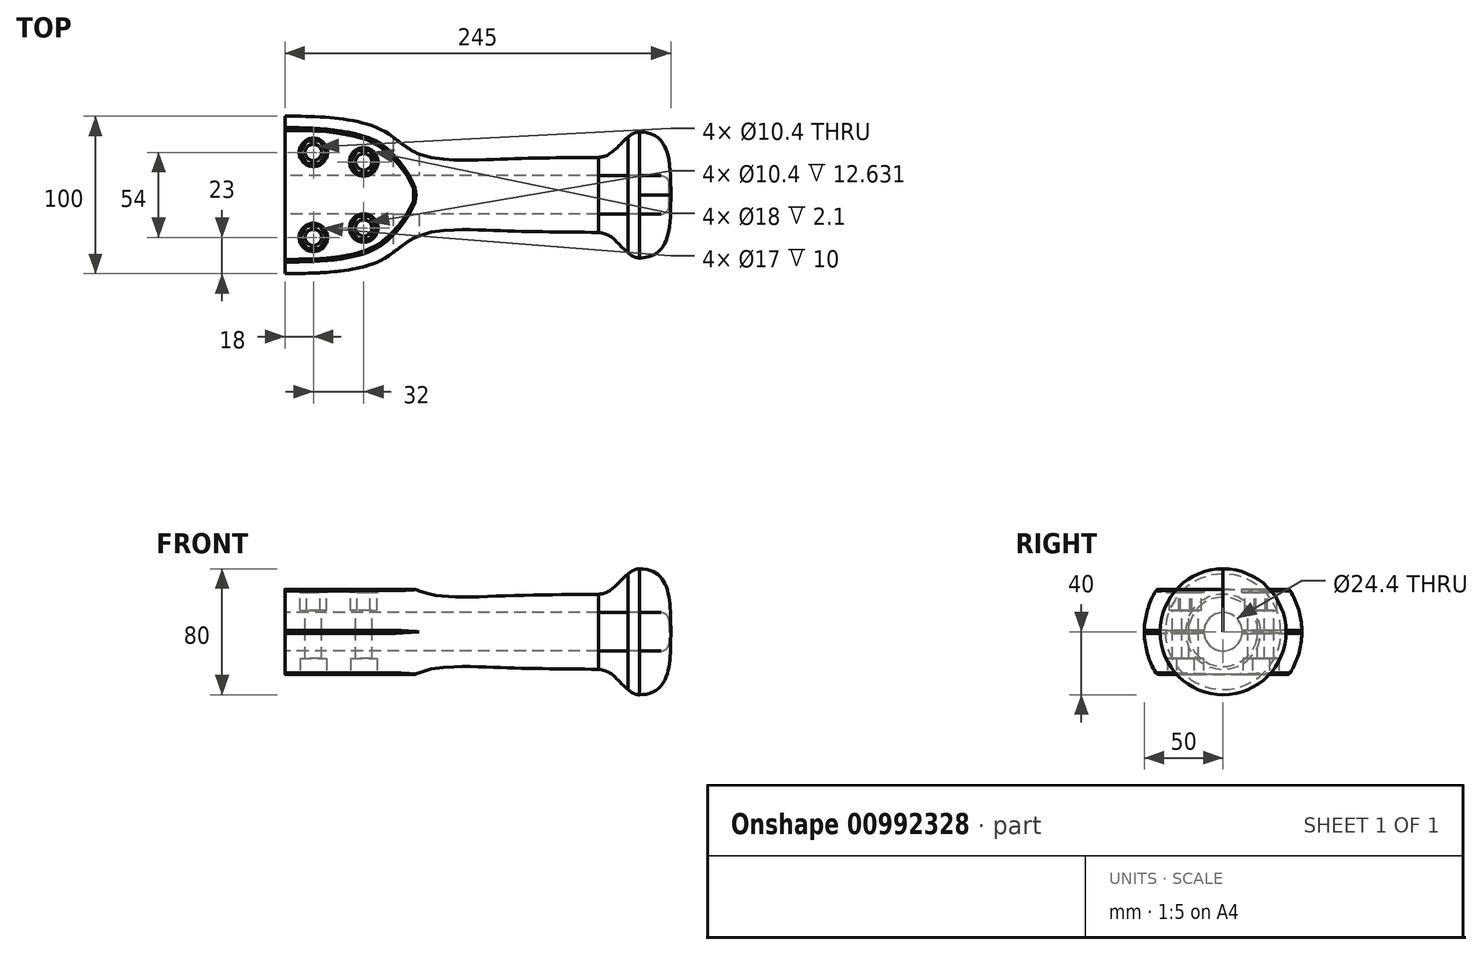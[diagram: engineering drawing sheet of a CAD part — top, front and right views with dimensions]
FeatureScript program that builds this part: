
annotation { "Feature Type Name" : "Feature", "Feature Type Description" : "" }
export const myFeature = defineFeature(function(context is Context, id is Id, definition is map)
    precondition{}
    {
        {
            var Q0;
            Q0=qCreatedBy(makeId("Front.planeOp"),FACE);
            var sketch = newSketch(context, id + "F0", { "sketchPlane" : qUnion([Q0])});
            skLineSegment(sketch, "E0", {"start": v(0, 50) * mm, "end": v(0, 0) * mm});
            skLineSegment(sketch, "E1", {"start": v(0, 0) * mm, "end": v(245, 0) * mm});
            skLineSegment(sketch, "E2", {"start": v(85, 0) * mm, "end": v(85, 26) * mm, "construction": true});
            skLineSegment(sketch, "E3", {"start": v(145, 0) * mm, "end": v(145, 23) * mm, "construction": true});
            skLineSegment(sketch, "E4", {"start": v(205, 0) * mm, "end": v(205, 24) * mm, "construction": true});
            skLineSegment(sketch, "E5", {"start": v(225, 0) * mm, "end": v(225, 40) * mm, "construction": true});
            skLineSegment(sketch, "E6", {"start": v(60, 42) * mm, "end": v(60, 0) * mm, "construction": true});
            skFitSpline(sketch, "E7", {"points": [v(0, 50) * mm, v(60, 42) * mm, v(85, 26) * mm, v(145, 23) * mm, v(205, 24) * mm], "startDerivative": vector(265.83, 0) * mm, "endDerivative": vector(46.28, 3.62) * mm});
            skLineSegment(sketch, "E8", {"start": v(85, 26) * mm, "end": v(85, 0) * mm});
            skLineSegment(sketch, "E9", {"start": v(0, 0) * mm, "end": v(85, 0) * mm});
            skLineSegment(sketch, "E10", {"start": v(205, 24) * mm, "end": v(205, 0) * mm});
            skPoint(sketch, "E11.middle", {"position": v(225, 0) * mm});
            skLineSegment(sketch, "E12.right", {"start": v(205, 15) * mm, "end": v(205, 0) * mm, "construction": true});
            skLineSegment(sketch, "E13", {"start": v(-11.82, 108.17) * mm, "end": v(-11.82, 58.17) * mm, "construction": true});
            skLineSegment(sketch, "E14", {"start": v(-11.82, 58.17) * mm, "end": v(233.18, 58.17) * mm, "construction": true});
            skLineSegment(sketch, "E15", {"start": v(73.18, 58.17) * mm, "end": v(73.18, 84.17) * mm, "construction": true});
            skLineSegment(sketch, "E16", {"start": v(133.18, 58.17) * mm, "end": v(133.18, 82.17) * mm, "construction": true});
            skLineSegment(sketch, "E17", {"start": v(48.18, 100.17) * mm, "end": v(48.18, 58.17) * mm, "construction": true});
            skFitSpline(sketch, "E18", {"points": [v(-11.82, 108.17) * mm, v(48.18, 100.17) * mm, v(73.18, 84.17) * mm, v(133.18, 82.17) * mm, v(193.18, 80.17) * mm], "startDerivative": vector(265.83, 0) * mm, "endDerivative": vector(46.66, -3.23) * mm, "construction": true});
            skLineSegment(sketch, "E19", {"start": v(73.18, 84.17) * mm, "end": v(73.18, 58.17) * mm, "construction": true});
            skLineSegment(sketch, "E20", {"start": v(-11.82, 58.17) * mm, "end": v(73.18, 58.17) * mm, "construction": true});
            skLineSegment(sketch, "E21", {"start": v(233.18, 58.17) * mm, "end": v(193.18, 58.17) * mm, "construction": true});
            skPoint(sketch, "E22.middle", {"position": v(213.18, 58.17) * mm});
            skLineSegment(sketch, "E23.bottom", {"start": v(227.18, 58.17) * mm, "end": v(233.18, 58.17) * mm, "construction": true});
            skLineSegment(sketch, "E24.right", {"start": v(193.18, 73.17) * mm, "end": v(193.18, 58.17) * mm, "construction": true});
            skFitSpline(sketch, "E25", {"points": [v(213.18, 98.17) * mm, v(233.18, 58.17) * mm], "startDerivative": vector(60, 0) * mm, "endDerivative": vector(0, -60) * mm, "construction": true});
            skLineSegment(sketch, "E26.top", {"start": v(213.18, 98.17) * mm, "end": v(233.18, 98.17) * mm, "construction": true});
            skLineSegment(sketch, "E26.left", {"start": v(213.18, 58.17) * mm, "end": v(213.18, 98.17) * mm, "construction": true});
            skLineSegment(sketch, "E26.right", {"start": v(233.18, 58.17) * mm, "end": v(233.18, 98.17) * mm, "construction": true});
            skFitSpline(sketch, "E27.MirrorCS", {"points": [v(213.18, 98.17) * mm, v(193.16, 58.15) * mm], "startDerivative": vector(-60, 0) * mm, "endDerivative": vector(-0.03, -60) * mm, "construction": true});
            skCircle(sketch, "E28", {"center": v(193.18, 80.17) * mm, "radius": 6 * mm, "construction": true});
            skFitSpline(sketch, "E29", {"points": [v(187.19, 80.56) * mm, v(195.66, 85.63) * mm], "startDerivative": vector(14.26, -0.68) * mm, "endDerivative": vector(2.5, 8.39) * mm, "construction": true});
            skLineSegment(sketch, "E30.bottom", {"start": v(213.18, 98.17) * mm, "end": v(193.18, 98.17) * mm, "construction": true});
            skLineSegment(sketch, "E30.top", {"start": v(213.18, 58.17) * mm, "end": v(193.18, 58.17) * mm, "construction": true});
            skLineSegment(sketch, "E30.left", {"start": v(213.18, 98.17) * mm, "end": v(213.18, 58.17) * mm, "construction": true});
            skLineSegment(sketch, "E31.bottom", {"start": v(193.18, 58.17) * mm, "end": v(233.17, 58.17) * mm, "construction": true});
            skLineSegment(sketch, "E31.top", {"start": v(193.18, 98.17) * mm, "end": v(233.18, 98.17) * mm, "construction": true});
            skLineSegment(sketch, "E31.right", {"start": v(233.17, 58.17) * mm, "end": v(233.18, 98.17) * mm, "construction": true});
            skLineSegment(sketch, "E32", {"start": v(193.18, 58.17) * mm, "end": v(233.18, 58.17) * mm, "construction": true});
            skFitSpline(sketch, "E33.MirrorCS", {"points": [v(213.18, 98.17) * mm, v(193.1, 58.17) * mm], "startDerivative": vector(-60, 0) * mm, "endDerivative": vector(0, -60) * mm, "construction": true});
            skFitSpline(sketch, "E34.MirrorCS", {"points": [v(213.18, 98.17) * mm, v(193.18, 58.17) * mm], "startDerivative": vector(-60, 0) * mm, "endDerivative": vector(0, -60) * mm, "construction": true});
            skLineSegment(sketch, "E35.bottom", {"start": v(245, 0) * mm, "end": v(205, 0) * mm, "construction": true});
            skLineSegment(sketch, "E35.top", {"start": v(245, 20) * mm, "end": v(205, 20) * mm, "construction": true});
            skLineSegment(sketch, "E35.left", {"start": v(245, 0) * mm, "end": v(245, 20) * mm, "construction": true});
            skLineSegment(sketch, "E35.right", {"start": v(205, 0) * mm, "end": v(205, 20) * mm, "construction": true});
            skLineSegment(sketch, "E36.bottom", {"start": v(225, 40) * mm, "end": v(245, 40) * mm, "construction": true});
            skLineSegment(sketch, "E36.top", {"start": v(225, 0) * mm, "end": v(245, 0) * mm, "construction": true});
            skLineSegment(sketch, "E36.left", {"start": v(225, 40) * mm, "end": v(225, 0) * mm, "construction": true});
            skLineSegment(sketch, "E36.right", {"start": v(245, 40) * mm, "end": v(245, 0) * mm, "construction": true});
            skFitSpline(sketch, "E37", {"points": [v(225, 40) * mm, v(245, 0) * mm], "startDerivative": vector(60, 0) * mm, "endDerivative": vector(0, -60) * mm});
            skLineSegment(sketch, "E38.bottom", {"start": v(225, 40) * mm, "end": v(205, 40) * mm, "construction": true});
            skLineSegment(sketch, "E38.top", {"start": v(225, 0) * mm, "end": v(205, 0) * mm, "construction": true});
            skLineSegment(sketch, "E38.right", {"start": v(205, 40) * mm, "end": v(205, 0) * mm, "construction": true});
            skCircle(sketch, "E39", {"center": v(195.66, 85.63) * mm, "radius": 2.92 * mm, "construction": true});
            skCircle(sketch, "E40", {"center": v(187.19, 80.56) * mm, "radius": 4.76 * mm, "construction": true});
            skFitSpline(sketch, "E41", {"points": [v(205, 0) * mm, v(225, 40) * mm], "startDerivative": vector(0, 60) * mm, "endDerivative": vector(30, 0) * mm});
            skFitSpline(sketch, "E42", {"points": [v(199, 23.84) * mm, v(217.81, 36.7) * mm], "startDerivative": vector(27.62, 1.67) * mm, "endDerivative": vector(18.82, 14.57) * mm});
            skLineSegment(sketch, "E43", {"start": v(217.81, 36.7) * mm, "end": v(180.43, -0.9) * mm, "construction": true});
            skLineSegment(sketch, "E44", {"start": v(214.8, 34.03) * mm, "end": v(210.87, 29.97) * mm, "construction": true});
            skLineSegment(sketch, "E45", {"start": v(205, 24) * mm, "end": v(79, 21.9) * mm, "construction": true});
            skLineSegment(sketch, "E46", {"start": v(79, 34.04) * mm, "end": v(79, 14.16) * mm, "construction": true});
            skLineSegment(sketch, "E47", {"start": v(106.67, 22.36) * mm, "end": v(107.04, 0) * mm, "construction": true});
            skLineSegment(sketch, "E48", {"start": v(107.04, 0) * mm, "end": v(106.67, 0.95) * mm, "construction": true});
            skSolve(sketch);
        }
        {
            var Q0;
            {var subQ0=sQuery(id+"F0.wireOp",EDGE,"E0");Q0=makeQuery(id+"F0.imprint","IMPRINT",FACE,{"disambiguationData":[TD([[makeQuery(id+"F0.imprint","IMPRINT",EDGE,{"derivedFrom":subQ0}),1.0]])]});}
            var Q1;
            {var subQ3=sQuery(id+"F0.wireOp",EDGE,"E8");Q1=makeQuery(id+"F0.imprint","IMPRINT",FACE,{"disambiguationData":[TD([[makeQuery(id+"F0.imprint","IMPRINT",EDGE,{"derivedFrom":subQ3}),1.0]])]});}
            var Q2;
            {var subQ0=sQuery(id+"F0.wireOp",EDGE,"E37");Q2=makeQuery(id+"F0.imprint","IMPRINT",FACE,{"disambiguationData":[TD([[makeQuery(id+"F0.imprint","IMPRINT",EDGE,{"derivedFrom":subQ0}),-1.0]])]});}
            var Q3;
            {var subQ0=sQuery(id+"F0.wireOp",EDGE,"E10");Q3=makeQuery(id+"F0.imprint","IMPRINT",FACE,{"disambiguationData":[TD([[makeQuery(id+"F0.imprint","IMPRINT",EDGE,{"derivedFrom":subQ0}),1.0]])]});}
            var Q4;
            Q4=sQuery(id+"F0.wireOp",EDGE,"E1");
            revolve(context, id + "F1", {"surfaceOperationType" : NewSurfaceOperationType.NEW, "entities" : qUnion([Q0, Q1, Q2, Q3]), "axis" : qUnion([Q4]), "revolveType" : RevolveType.FULL});
        }
        {
            var Q0;
            Q0=qCreatedBy(makeId("Right.planeOp"),FACE);
            cPlane(context, id + "F2", {"entities" : qUnion([Q0]), "cplaneType" : CPlaneType.OFFSET, "offset" : 90 * mm, "width" : 150 * mm, "height" : 150 * mm});
        }
        {
            var Q0;
            Q0=qCreatedBy(id+"F2.planeOp",FACE);
            var sketch = newSketch(context, id + "F3", { "sketchPlane" : qUnion([Q0])});
            skLineSegment(sketch, "E49.bottom", {"start": v(-65.87, 27) * mm, "end": v(58.89, 27) * mm});
            skLineSegment(sketch, "E49.top", {"start": v(-65.87, -27) * mm, "end": v(58.89, -27) * mm});
            skLineSegment(sketch, "E49.left", {"start": v(-65.87, 27) * mm, "end": v(-65.87, -27) * mm});
            skLineSegment(sketch, "E49.right", {"start": v(58.89, 27) * mm, "end": v(58.89, -27) * mm});
            skPoint(sketch, "E49.middle", {"position": v(-3.5, 0) * mm});
            skLineSegment(sketch, "E50.bottom", {"start": v(-135.82, 62.52) * mm, "end": v(135.82, 62.52) * mm});
            skLineSegment(sketch, "E50.top", {"start": v(-135.82, -80.38) * mm, "end": v(135.82, -80.38) * mm});
            skLineSegment(sketch, "E50.left", {"start": v(-135.82, 62.52) * mm, "end": v(-135.82, -80.38) * mm});
            skLineSegment(sketch, "E50.right", {"start": v(135.82, 62.52) * mm, "end": v(135.82, -80.38) * mm});
            skPoint(sketch, "E50.middle", {"position": v(0, -8.93) * mm});
            skSolve(sketch);
        }
        {
            var Q0;
            Q0=makeQuery(id+"F3.imprint","IMPRINT",FACE,{"disambiguationData":[TD([[makeQuery(id+"F3.imprint","IMPRINT",EDGE,{"derivedFrom":sQuery(id+"F3.wireOp",EDGE,"E49.bottom")}),1.0]])]});
            extrude(context, id + "F4", {"entities" : qUnion([Q0]), "operationType" : NewBodyOperationType.REMOVE, "oppositeDirection" : true, "depth" : 139 * mm, "offsetDistance" : 25 * mm});
        }
        {
            var Q0;
            Q0=makeQuery(id+"F4.boolean.opBoolean","INTERSECT",EDGE,{"derivedFrom":[makeQuery(id+"F1.opRevolve","SWEPT_FACE",FACE,{"disambiguationData":[OSD([sQuery(id+"F0.wireOp",EDGE,"E7")])]}),makeQuery(id+"F4.opExtrude","SWEPT_FACE",FACE,{"disambiguationData":[OSD([sQuery(id+"F3.wireOp",EDGE,"E49.bottom")])]})]});
            var Q1;
            Q1=makeQuery(id+"F4.boolean.opBoolean","INTERSECT",EDGE,{"derivedFrom":[makeQuery(id+"F1.opRevolve","SWEPT_FACE",FACE,{"disambiguationData":[OSD([sQuery(id+"F0.wireOp",EDGE,"E7")])]}),makeQuery(id+"F4.opExtrude","SWEPT_FACE",FACE,{"disambiguationData":[OSD([sQuery(id+"F3.wireOp",EDGE,"E49.top")])]})]});
            fillet(context, id + "F5", {"entities" : qUnion([Q0, Q1]), "radius" : 2 * mm, "tangentPropagation" : true, "defaultsChanged" : true, "vertexSettings" : [], "allowEdgeOverflow" : false});
        }
        {
            var Q0;
            Q0=makeQuery(id+"F4.boolean.opBoolean","COPY",FACE,{"derivedFrom":makeQuery(id+"F4.opExtrude","SWEPT_FACE",FACE,{"disambiguationData":[OSD([sQuery(id+"F3.wireOp",EDGE,"E49.bottom")])]})});
            var sketch = newSketch(context, id + "F6", { "sketchPlane" : qUnion([Q0])});
            skLineSegment(sketch, "E51", {"start": v(0, 0) * mm, "end": v(79.24, 0) * mm, "construction": true});
            skCircle(sketch, "E52.cCircle", {"center": v(50, 21) * mm, "radius": 7.2 * mm, "construction": true});
            skLineSegment(sketch, "E52.0", {"start": v(54.16, 28.2) * mm, "end": v(58.31, 21) * mm});
            skLineSegment(sketch, "E52.1", {"start": v(58.31, 21) * mm, "end": v(54.16, 13.8) * mm});
            skLineSegment(sketch, "E52.2", {"start": v(54.16, 13.8) * mm, "end": v(45.84, 13.8) * mm});
            skLineSegment(sketch, "E52.3", {"start": v(45.84, 13.8) * mm, "end": v(41.69, 21) * mm});
            skLineSegment(sketch, "E52.4", {"start": v(41.69, 21) * mm, "end": v(45.84, 28.2) * mm});
            skLineSegment(sketch, "E52.5", {"start": v(45.84, 28.2) * mm, "end": v(54.16, 28.2) * mm});
            skPoint(sketch, "E52.0.midPoint", {"position": v(56.24, 24.6) * mm});
            skCircle(sketch, "E53.cCircle", {"center": v(18, 27) * mm, "radius": 7.2 * mm, "construction": true});
            skLineSegment(sketch, "E53.0", {"start": v(13.84, 34.2) * mm, "end": v(22.16, 34.2) * mm});
            skLineSegment(sketch, "E53.1", {"start": v(22.16, 34.2) * mm, "end": v(26.31, 27) * mm});
            skLineSegment(sketch, "E53.2", {"start": v(26.31, 27) * mm, "end": v(22.16, 19.8) * mm});
            skLineSegment(sketch, "E53.3", {"start": v(22.16, 19.8) * mm, "end": v(13.84, 19.8) * mm});
            skLineSegment(sketch, "E53.4", {"start": v(13.84, 19.8) * mm, "end": v(9.69, 27) * mm});
            skLineSegment(sketch, "E53.5", {"start": v(9.69, 27) * mm, "end": v(13.84, 34.2) * mm});
            skPoint(sketch, "E53.0.midPoint", {"position": v(18, 34.2) * mm});
            skPoint(sketch, "E54.cCircle.perimeterSnap0", {"position": v(24.24, 30.6) * mm});
            skPoint(sketch, "E54.0.midPoint.positionSnap0", {"position": v(24.24, 30.6) * mm});
            skFitSpline(sketch, "E55.0", {"points": [v(0, -39.26) * mm, v(4.13, -39.26) * mm, v(10.34, -39.2) * mm, v(18.6, -38.88) * mm, v(24.78, -38.5) * mm, v(30.96, -37.92) * mm, v(36.08, -37.22) * mm, v(40.14, -36.5) * mm, v(43.17, -35.87) * mm, v(45.68, -35.24) * mm, v(47.67, -34.67) * mm, v(49.65, -34.05) * mm, v(52.07, -33.19) * mm, v(54.9, -31.97) * mm, v(57.18, -30.78) * mm, v(58.94, -29.69) * mm, v(60.23, -28.8) * mm, v(61.47, -27.86) * mm, v(63.08, -26.55) * mm, v(64.98, -24.82) * mm, v(67.15, -22.63) * mm, v(69.24, -20.36) * mm, v(71.26, -18.02) * mm, v(73.24, -15.64) * mm, v(75.17, -13.21) * mm, v(77.03, -10.74) * mm, v(78.5, -8.61) * mm, v(79.56, -6.84) * mm, v(80.28, -5.46) * mm, v(80.9, -4.04) * mm, v(81.29, -2.8) * mm, v(81.5, -1.78) * mm, v(81.65, -0.76) * mm, v(81.68, 0.53) * mm, v(81.48, 2.09) * mm, v(81.06, 3.58) * mm, v(80.5, 5.01) * mm, v(79.8, 6.41) * mm, v(79.02, 7.75) * mm, v(77.92, 9.47) * mm, v(76.43, 11.56) * mm, v(74.56, 14) * mm, v(72.62, 16.4) * mm, v(70.64, 18.75) * mm, v(68.6, 21.06) * mm, v(66.5, 23.3) * mm, v(64.32, 25.45) * mm, v(62.4, 27.13) * mm, v(60.78, 28.4) * mm, v(59.52, 29.3) * mm, v(58.21, 30.15) * mm, v(56.88, 30.92) * mm, v(55.53, 31.63) * mm, v(53.69, 32.5) * mm, v(51.34, 33.47) * mm, v(48.46, 34.45) * mm, v(45.52, 35.3) * mm, v(42.53, 36.01) * mm, v(39.52, 36.62) * mm, v(35.5, 37.3) * mm, v(30.46, 37.97) * mm, v(22.37, 38.7) * mm, v(12.22, 39.17) * mm, v(4.07, 39.26) * mm, v(0, 39.26) * mm]});
            skLineSegment(sketch, "E56.bottom", {"start": v(50, 21) * mm, "end": v(18, 21) * mm, "construction": true});
            skLineSegment(sketch, "E57.MirrorCS", {"start": v(54.16, -28.2) * mm, "end": v(58.31, -21) * mm});
            skPoint(sketch, "E58.MirrorP", {"position": v(24.24, -30.6) * mm});
            skLineSegment(sketch, "E59.MirrorCS", {"start": v(41.69, -21) * mm, "end": v(45.84, -28.2) * mm});
            skPoint(sketch, "E60.MirrorP", {"position": v(18, -34.2) * mm});
            skLineSegment(sketch, "E61.MirrorCS", {"start": v(13.84, -34.2) * mm, "end": v(22.16, -34.2) * mm});
            skLineSegment(sketch, "E62.MirrorCS", {"start": v(9.69, -27) * mm, "end": v(13.84, -34.2) * mm});
            skLineSegment(sketch, "E63.MirrorCS", {"start": v(22.16, -19.8) * mm, "end": v(13.84, -19.8) * mm});
            skLineSegment(sketch, "E64.MirrorCS", {"start": v(45.84, -13.8) * mm, "end": v(41.69, -21) * mm});
            skPoint(sketch, "E65.MirrorP", {"position": v(56.24, -24.6) * mm});
            skLineSegment(sketch, "E66.MirrorCS", {"start": v(54.16, -13.8) * mm, "end": v(45.84, -13.8) * mm});
            skLineSegment(sketch, "E67.MirrorCS", {"start": v(58.31, -21) * mm, "end": v(54.16, -13.8) * mm});
            skLineSegment(sketch, "E68.MirrorCS", {"start": v(50, -21) * mm, "end": v(18, -21) * mm, "construction": true});
            skLineSegment(sketch, "E69.MirrorCS", {"start": v(13.84, -19.8) * mm, "end": v(9.69, -27) * mm});
            skCircle(sketch, "E70.MirrorC", {"center": v(18, -27) * mm, "radius": 7.2 * mm, "construction": true});
            skLineSegment(sketch, "E71.MirrorCS", {"start": v(22.16, -34.2) * mm, "end": v(26.31, -27) * mm});
            skLineSegment(sketch, "E72.MirrorCS", {"start": v(26.31, -27) * mm, "end": v(22.16, -19.8) * mm});
            skCircle(sketch, "E73.MirrorC", {"center": v(50, -21) * mm, "radius": 7.2 * mm, "construction": true});
            skLineSegment(sketch, "E74.MirrorCS", {"start": v(45.84, -28.2) * mm, "end": v(54.16, -28.2) * mm});
            skSolve(sketch);
        }
        {
            var Q0;
            Q0=qSketchRegion(id+"F6",true);
            extrude(context, id + "F7", {"entities" : qUnion([Q0]), "operationType" : NewBodyOperationType.REMOVE, "oppositeDirection" : true, "depth" : 13.4 * mm, "offsetDistance" : 25 * mm});
        }
        {
            var Q0;
            Q0=makeQuery(id+"F4.boolean.opBoolean","COPY",FACE,{"derivedFrom":makeQuery(id+"F4.opExtrude","SWEPT_FACE",FACE,{"disambiguationData":[OSD([sQuery(id+"F3.wireOp",EDGE,"E49.bottom")])]})});
            var sketch = newSketch(context, id + "F8", { "sketchPlane" : qUnion([Q0])});
            skCircle(sketch, "E75.20", {"center": v(18, 27) * mm, "radius": 9 * mm});
            skCircle(sketch, "E75.21", {"center": v(50, 21) * mm, "radius": 9 * mm});
            skLineSegment(sketch, "E76", {"start": v(0, 0) * mm, "end": v(82.32, 0) * mm, "construction": true});
            skCircle(sketch, "E77.MirrorC", {"center": v(18, -27) * mm, "radius": 9 * mm});
            skCircle(sketch, "E78.MirrorC", {"center": v(50, -21) * mm, "radius": 9 * mm});
            skLineSegment(sketch, "E79", {"start": v(13.84, 34.2) * mm, "end": v(22.16, 19.8) * mm, "construction": true});
            skLineSegment(sketch, "E80", {"start": v(45.84, 28.2) * mm, "end": v(54.16, 13.8) * mm, "construction": true});
            skSolve(sketch);
        }
        {
            var Q0;
            Q0=qSketchRegion(id+"F8",true);
            extrude(context, id + "F9", {"entities" : qUnion([Q0]), "operationType" : NewBodyOperationType.REMOVE, "oppositeDirection" : true, "depth" : 2.1 * mm, "offsetDistance" : 25 * mm});
        }
        {
            var Q0;
            Q0=makeQuery(id+"F4.boolean.opBoolean","COPY",FACE,{"derivedFrom":makeQuery(id+"F4.opExtrude","SWEPT_FACE",FACE,{"disambiguationData":[OSD([sQuery(id+"F3.wireOp",EDGE,"E49.bottom")])]})});
            var sketch = newSketch(context, id + "F10", { "sketchPlane" : qUnion([Q0])});
            skCircle(sketch, "E81.0", {"center": v(18, 27) * mm, "radius": 9 * mm, "construction": true});
            skCircle(sketch, "E82.0", {"center": v(50, 21) * mm, "radius": 9 * mm, "construction": true});
            skCircle(sketch, "E83", {"center": v(18, 27) * mm, "radius": 5.2 * mm});
            skCircle(sketch, "E84", {"center": v(50, 21) * mm, "radius": 5.2 * mm});
            skLineSegment(sketch, "E85", {"start": v(0, 0) * mm, "end": v(82.32, 0) * mm, "construction": true});
            skCircle(sketch, "E86.MirrorC", {"center": v(18, -27) * mm, "radius": 5.2 * mm});
            skCircle(sketch, "E87.MirrorC", {"center": v(50, -21) * mm, "radius": 5.2 * mm});
            skSolve(sketch);
        }
        {
            var Q0;
            Q0=qSketchRegion(id+"F10",true);
            extrude(context, id + "F11", {"entities" : qUnion([Q0]), "operationType" : NewBodyOperationType.REMOVE, "endBound" : BoundingType.THROUGH_ALL, "oppositeDirection" : true, "depth" : 25 * mm, "offsetDistance" : 25 * mm});
        }
        {
            var Q0;
            Q0=makeQuery(id+"F4.boolean.opBoolean","COPY",FACE,{"derivedFrom":makeQuery(id+"F4.opExtrude","SWEPT_FACE",FACE,{"disambiguationData":[OSD([sQuery(id+"F3.wireOp",EDGE,"E49.top")])]})});
            var sketch = newSketch(context, id + "F12", { "sketchPlane" : qUnion([Q0])});
            skCircle(sketch, "E88.0", {"center": v(50, -21) * mm, "radius": 5.2 * mm, "construction": true});
            skCircle(sketch, "E88.1", {"center": v(18, -27) * mm, "radius": 5.2 * mm, "construction": true});
            skCircle(sketch, "E88.2", {"center": v(18, -27) * mm, "radius": 5.2 * mm, "construction": true});
            skCircle(sketch, "E88.3", {"center": v(18, -27) * mm, "radius": 5.2 * mm, "construction": true});
            skCircle(sketch, "E89", {"center": v(18, -27) * mm, "radius": 8.5 * mm});
            skCircle(sketch, "E90", {"center": v(50, -21) * mm, "radius": 8.5 * mm});
            skLineSegment(sketch, "E91", {"start": v(0, 0) * mm, "end": v(82.32, 0) * mm, "construction": true});
            skLineSegment(sketch, "E92", {"start": v(82.32, 0) * mm, "end": v(80.56, 1.17) * mm, "construction": true});
            skCircle(sketch, "E93.MirrorC", {"center": v(18, 27) * mm, "radius": 8.5 * mm});
            skCircle(sketch, "E94.MirrorC", {"center": v(50, 21) * mm, "radius": 8.5 * mm});
            skSolve(sketch);
        }
        {
            var Q0;
            Q0=qSketchRegion(id+"F12",true);
            extrude(context, id + "F13", {"entities" : qUnion([Q0]), "operationType" : NewBodyOperationType.REMOVE, "oppositeDirection" : true, "depth" : 10 * mm, "offsetDistance" : 25 * mm});
        }
        {
            var Q0;
            Q0=qCreatedBy(makeId("Front.planeOp"),FACE);
            var sketch = newSketch(context, id + "F14", { "sketchPlane" : qUnion([Q0])});
            skLineSegment(sketch, "E95.bottom", {"start": v(68.64, 0.97) * mm, "end": v(-85.25, 0.97) * mm});
            skLineSegment(sketch, "E95.top", {"start": v(68.64, -0.97) * mm, "end": v(-84.75, -0.97) * mm});
            skLineSegment(sketch, "E95.right", {"start": v(-85.25, 0.97) * mm, "end": v(-84.75, -0.97) * mm});
            skPoint(sketch, "E95.middle", {"position": v(0, 0) * mm});
            skLineSegment(sketch, "E96", {"start": v(0, 0) * mm, "end": v(85, 0) * mm, "construction": true});
            skFitSpline(sketch, "E97", {"points": [v(85, 0) * mm, v(68.64, -0.97) * mm], "startDerivative": vector(-9.95, -0.23) * mm, "endDerivative": vector(-4.19, 0.16) * mm});
            skFitSpline(sketch, "E98.MirrorCS", {"points": [v(85, 0) * mm, v(68.64, 0.97) * mm], "startDerivative": vector(-9.95, 0.23) * mm, "endDerivative": vector(-4.19, -0.16) * mm});
            skPoint(sketch, "E99.orphan", {"position": v(85.25, -0.97) * mm});
            skPoint(sketch, "E95.left.start.orphan", {"position": v(84.75, 0.97) * mm});
            skSolve(sketch);
        }
        {
            var Q0;
            Q0=qSketchRegion(id+"F14",true);
            extrude(context, id + "F15", {"entities" : qUnion([Q0]), "operationType" : NewBodyOperationType.REMOVE, "endBound" : BoundingType.SYMMETRIC, "oppositeDirection" : true, "depth" : 120 * mm, "offsetDistance" : 25 * mm});
        }
        {
            var Q0;
            {var subQ1=sQuery(id+"F3.wireOp",EDGE,"E49.top");Q0=makeQuery(id+"F15.boolean.opBoolean","SPLIT",FACE,{"disambiguationData":[TD([makeQuery(id+"F4.boolean.opBoolean","COPY",FACE,{"derivedFrom":makeQuery(id+"F4.opExtrude","SWEPT_FACE",FACE,{"disambiguationData":[OSD([subQ1])]})})])],"derivedFrom":makeQuery(id+"F1.opRevolve","SWEPT_FACE",FACE,{"disambiguationData":[OSD([sQuery(id+"F0.wireOp",EDGE,"E0")])]})});}
            var sketch = newSketch(context, id + "F16", { "sketchPlane" : qUnion([Q0])});
            skCircle(sketch, "E100", {"center": v(0, 0) * mm, "radius": 12.2 * mm});
            skSolve(sketch);
        }
        {
            var Q0;
            Q0=qSketchRegion(id+"F16",true);
            extrude(context, id + "F17", {"entities" : qUnion([Q0]), "operationType" : NewBodyOperationType.REMOVE, "oppositeDirection" : true, "depth" : 243.8 * mm, "offsetDistance" : 25 * mm});
        }
        {
            var Q0;
            {var subQ1=sQuery(id+"F3.wireOp",EDGE,"E49.bottom");Q0=makeQuery(id+"F15.boolean.opBoolean","SPLIT",FACE,{"disambiguationData":[TD([makeQuery(id+"F4.boolean.opBoolean","COPY",FACE,{"derivedFrom":makeQuery(id+"F4.opExtrude","SWEPT_FACE",FACE,{"disambiguationData":[OSD([subQ1])]})})])],"derivedFrom":makeQuery(id+"F1.opRevolve","SWEPT_FACE",FACE,{"disambiguationData":[OSD([sQuery(id+"F0.wireOp",EDGE,"E0")])]})});}
            var sketch = newSketch(context, id + "F18", { "sketchPlane" : qUnion([Q0])});
            skArc(sketch, "E101", {"start": v(-50, 0.97) * mm, "mid": v(-50, 0) * mm, "end": v(-50, -0.97) * mm});
            skArc(sketch, "E102", {"start": v(-49.2, 0.97) * mm, "mid": v(-49.2, 0) * mm, "end": v(-49.2, -0.97) * mm});
            skLineSegment(sketch, "E103.bottom", {"start": v(50, 0.97) * mm, "end": v(49.2, 0.97) * mm});
            skLineSegment(sketch, "E103.top", {"start": v(50, -0.97) * mm, "end": v(49.2, -0.97) * mm});
            skLineSegment(sketch, "E103.right", {"start": v(-50, 0.97) * mm, "end": v(-50, -0.97) * mm});
            skLineSegment(sketch, "E104.trimOffspring", {"start": v(-49.2, 0.97) * mm, "end": v(-50, 0.97) * mm});
            skLineSegment(sketch, "E105.trimOffspring", {"start": v(-49.2, -0.97) * mm, "end": v(-50, -0.97) * mm});
            skArc(sketch, "E106.trimOffspring", {"start": v(49.2, -0.97) * mm, "mid": v(49.2, 0) * mm, "end": v(49.2, 0.97) * mm});
            skArc(sketch, "E107.trimOffspring", {"start": v(50, -0.97) * mm, "mid": v(50, 0) * mm, "end": v(50, 0.97) * mm});
            skSolve(sketch);
        }
        {
            var Q0;
            Q0 = qSketchRegion(id + "F18", true);
            extrude(context, id + "F19", {"entities" : qUnion([Q0]), "operationType" : NewBodyOperationType.ADD, "oppositeDirection" : true, "depth" : .3 * mm, "offsetDistance" : 25 * mm});
        }
        {
            var Q0;
            Q0=makeQuery(id+"F17.boolean.opBoolean","COPY",EDGE,{"derivedFrom":makeQuery(id+"F17.opExtrude","CAP_EDGE",EDGE,{"disambiguationData":[OSD([sQuery(id+"F16.wireOp",EDGE,"E100")])],"isStart":false})});
            fillet(context, id + "F20", {"entities" : qUnion([Q0]), "tangentPropagation" : true, "radius" : 5 * mm, "defaultsChanged" : false, "vertexSettings" : [], "allowEdgeOverflow" : false});
        }
    });
